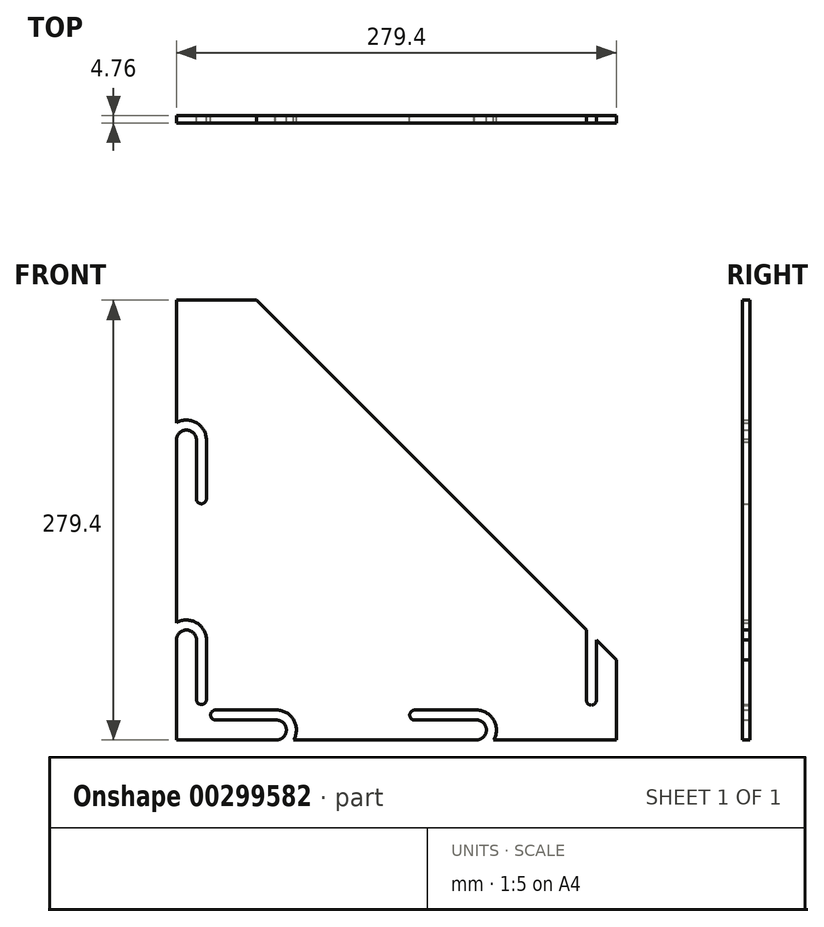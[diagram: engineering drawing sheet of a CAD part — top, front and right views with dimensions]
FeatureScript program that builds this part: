
annotation { "Feature Type Name" : "Feature", "Feature Type Description" : "" }
export const myFeature = defineFeature(function(context is Context, id is Id, definition is map)
    precondition{}
    {
        {
            var Q0;
            Q0=qCreatedBy(makeId("Front.planeOp"),FACE);
            var sketch = newSketch(context, id + "F0", { "sketchPlane" : qUnion([Q0])});
            skLineSegment(sketch, "E0.bottom", {"start": v(-117.22, 228.6) * mm, "end": v(-66.42, 228.6) * mm});
            skLineSegment(sketch, "E0.top", {"start": v(-117.22, -50.8) * mm, "end": v(-53.72, -50.8) * mm});
            skLineSegment(sketch, "E0.left", {"start": v(-117.22, 228.6) * mm, "end": v(-117.22, 150.7) * mm});
            skLineSegment(sketch, "E0.right", {"start": v(162.18, 0) * mm, "end": v(162.18, -50.8) * mm});
            skLineSegment(sketch, "E1", {"start": v(-66.42, 228.6) * mm, "end": v(143.13, 19.05) * mm});
            skArc(sketch, "E2", {"start": v(-53.72, -50.8) * mm, "mid": v(-47.37, -44.19) * mm, "end": v(-54.24, -38.12) * mm});
            skArc(sketch, "E3", {"start": v(73.28, -50.8) * mm, "mid": v(79.61, -43.91) * mm, "end": v(72.2, -38.2) * mm});
            skArc(sketch, "E4", {"start": v(-104.56, 138.91) * mm, "mid": v(-110.47, 146.04) * mm, "end": v(-117.22, 139.7) * mm});
            skArc(sketch, "E5", {"start": v(-104.52, 12.42) * mm, "mid": v(-110.73, 19.05) * mm, "end": v(-117.22, 12.7) * mm});
            skLineSegment(sketch, "E6", {"start": v(-104.56, 140.49) * mm, "end": v(-104.56, 102.39) * mm});
            skLineSegment(sketch, "E7", {"start": v(-104.52, 12.98) * mm, "end": v(-104.52, -25.12) * mm});
            skLineSegment(sketch, "E8", {"start": v(-54.24, -38.12) * mm, "end": v(-92.34, -38.12) * mm});
            skLineSegment(sketch, "E9", {"start": v(72.2, -38.2) * mm, "end": v(34.1, -38.2) * mm});
            skLineSegment(sketch, "E10", {"start": v(149.48, 12.7) * mm, "end": v(149.48, -25.5) * mm});
            skLineSegment(sketch, "E11", {"start": v(143.13, 19.05) * mm, "end": v(143.13, -25.5) * mm});
            skArc(sketch, "E12", {"start": v(143.13, -25.5) * mm, "mid": v(146.3, -28.68) * mm, "end": v(149.48, -25.5) * mm});
            skLineSegment(sketch, "E13.trimOffspring", {"start": v(149.48, 12.7) * mm, "end": v(162.18, 0) * mm});
            skLineSegment(sketch, "E14.0", {"start": v(72.2, -31.84) * mm, "end": v(34.1, -31.84) * mm});
            skLineSegment(sketch, "E15.0", {"start": v(-54.24, -31.77) * mm, "end": v(-92.34, -31.77) * mm});
            skLineSegment(sketch, "E16.0", {"start": v(-98.17, 12.98) * mm, "end": v(-98.17, -25.12) * mm});
            skLineSegment(sketch, "E17.0", {"start": v(-98.21, 140.49) * mm, "end": v(-98.21, 102.39) * mm});
            skArc(sketch, "E18", {"start": v(-104.56, 102.39) * mm, "mid": v(-101.39, 99.21) * mm, "end": v(-98.21, 102.39) * mm});
            skArc(sketch, "E19", {"start": v(-104.52, -25.12) * mm, "mid": v(-101.35, -28.3) * mm, "end": v(-98.17, -25.12) * mm});
            skArc(sketch, "E20", {"start": v(-92.34, -31.77) * mm, "mid": v(-95.52, -34.95) * mm, "end": v(-92.34, -38.12) * mm});
            skArc(sketch, "E21", {"start": v(34.1, -31.84) * mm, "mid": v(30.93, -35.02) * mm, "end": v(34.1, -38.2) * mm});
            skArc(sketch, "E22.0", {"start": v(84.28, -50.8) * mm, "mid": v(83.7, -37.19) * mm, "end": v(71.13, -31.93) * mm});
            skArc(sketch, "E23.0", {"start": v(-42.72, -50.8) * mm, "mid": v(-43, -37.65) * mm, "end": v(-54.77, -31.8) * mm});
            skArc(sketch, "E24.0", {"start": v(-98.18, 12.14) * mm, "mid": v(-104.28, 23.56) * mm, "end": v(-117.22, 23.7) * mm});
            skArc(sketch, "E25.0", {"start": v(-98.26, 138.12) * mm, "mid": v(-103.84, 150.28) * mm, "end": v(-117.22, 150.7) * mm});
            skLineSegment(sketch, "E26.trimOffspring", {"start": v(-117.22, 139.7) * mm, "end": v(-117.22, 23.7) * mm});
            skLineSegment(sketch, "E27.trimOffspring", {"start": v(-42.72, -50.8) * mm, "end": v(73.28, -50.8) * mm});
            skLineSegment(sketch, "E28.trimOffspring", {"start": v(-117.22, 12.7) * mm, "end": v(-117.22, -50.8) * mm});
            skLineSegment(sketch, "E29.trimOffspring", {"start": v(84.28, -50.8) * mm, "end": v(162.18, -50.8) * mm});
            skSolve(sketch);
        }
        {
            var Q0;
            Q0=makeQuery(id+"F0.imprint","IMPRINT",FACE,{"disambiguationData":[TD([[makeQuery(id+"F0.imprint","IMPRINT",EDGE,{"derivedFrom":sQuery(id+"F0.wireOp",EDGE,"E0.bottom")}),-1.0]])]});
            extrude(context, id + "F1", {"entities" : qUnion([Q0]), "depth" : 4.76 * mm});
        }
    });
